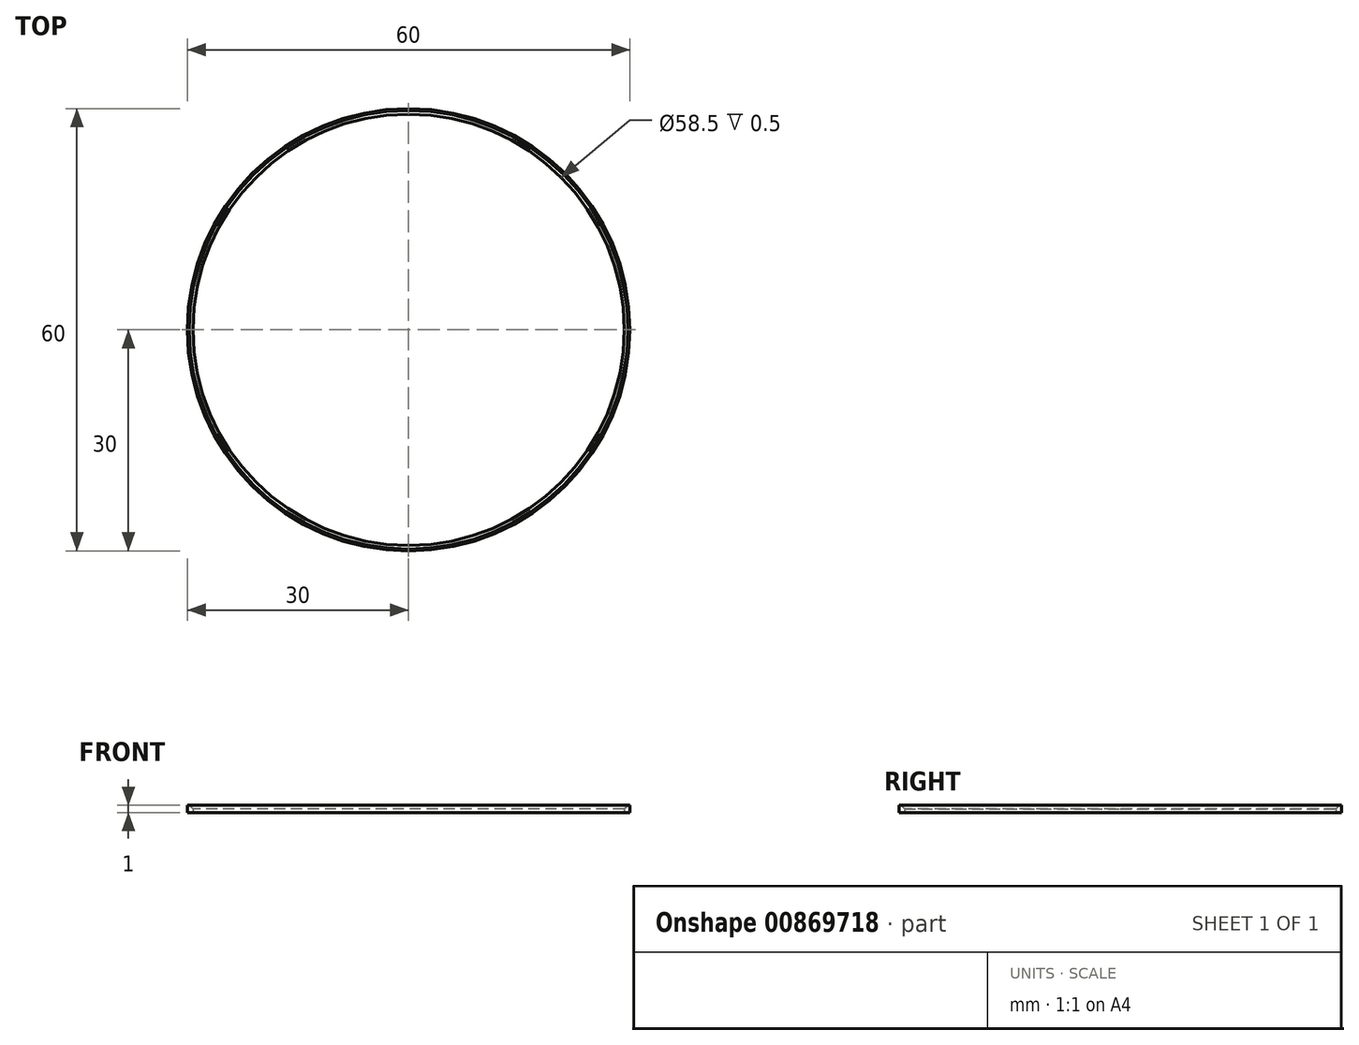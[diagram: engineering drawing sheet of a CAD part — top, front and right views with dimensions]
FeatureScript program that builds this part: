
annotation { "Feature Type Name" : "Feature", "Feature Type Description" : "" }
export const myFeature = defineFeature(function(context is Context, id is Id, definition is map)
    precondition{}
    {
        {
            var Q0;
            Q0=qCreatedBy(makeId("Top.planeOp"),FACE);
            var sketch = newSketch(context, id + "F0", { "sketchPlane" : qUnion([Q0])});
            skArc(sketch, "E0", {"start": v(0, 30) * mm, "mid": v(21.21, 21.21) * mm, "end": v(30, 0) * mm});
            skArc(sketch, "E1", {"start": v(30, 0) * mm, "mid": v(21.21, -21.21) * mm, "end": v(0, -30) * mm});
            skArc(sketch, "E2", {"start": v(0, -30) * mm, "mid": v(-21.21, -21.21) * mm, "end": v(-30, 0) * mm});
            skArc(sketch, "E3", {"start": v(-30, 0) * mm, "mid": v(-21.21, 21.21) * mm, "end": v(0, 30) * mm});
            skCircle(sketch, "E4", {"center": v(0, 0) * mm, "radius": 29.25 * mm});
            skSolve(sketch);
        }
        {
            var Q0;
            Q0 = qSketchRegion(id + "F0", true);
            extrude(context, id + "F1", {"entities" : qUnion([Q0]), "depth" : 1 * mm, "offsetDistance" : 25 * mm});
        }
        {
            var Q0;
            Q0=makeQuery(id+"F1.opExtrude","CAP_EDGE",EDGE,{"disambiguationData":[OSD([sQuery(id+"F0.wireOp",EDGE,"E4")])],"isStart":false});
            chamfer(context, id + "F2", {"entities" : qUnion([Q0]), "width" : .5 * mm, "tangentPropagation" : true});
        }
    });
